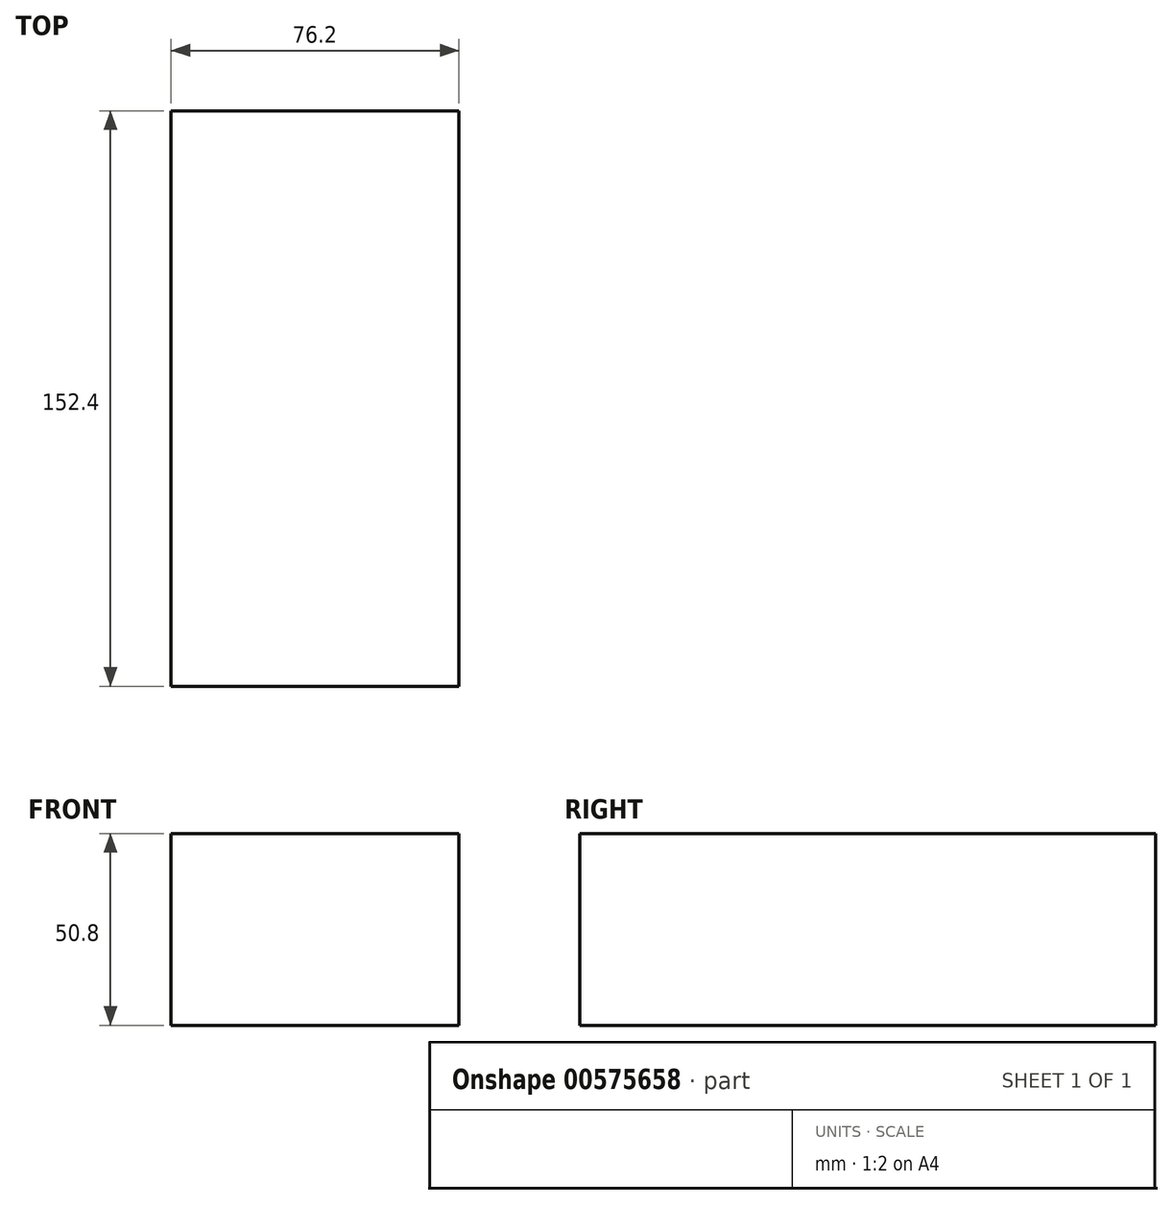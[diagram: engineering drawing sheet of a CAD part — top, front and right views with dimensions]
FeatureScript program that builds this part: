
annotation { "Feature Type Name" : "Feature", "Feature Type Description" : "" }
export const myFeature = defineFeature(function(context is Context, id is Id, definition is map)
    precondition{}
    {
        {
            var Q0;
            Q0=qCreatedBy(makeId("Front.planeOp"),FACE);
            var sketch = newSketch(context, id + "F0", { "sketchPlane" : qUnion([Q0])});
            skLineSegment(sketch, "E0.bottom", {"start": v(-45.07, -32.82) * mm, "end": v(31.13, -32.82) * mm});
            skLineSegment(sketch, "E0.top", {"start": v(-45.07, 17.98) * mm, "end": v(31.13, 17.98) * mm});
            skLineSegment(sketch, "E0.left", {"start": v(-45.07, -32.82) * mm, "end": v(-45.07, 17.98) * mm});
            skLineSegment(sketch, "E0.right", {"start": v(31.13, -32.82) * mm, "end": v(31.13, 17.98) * mm});
            skSolve(sketch);
        }
        {
            var Q0;
            Q0 = qSketchRegion(id + "F0", true);
            extrude(context, id + "F1", {"entities" : qUnion([Q0]), "depth" : 152.4 * mm, "offsetDistance" : 25.4 * mm});
        }
    });
